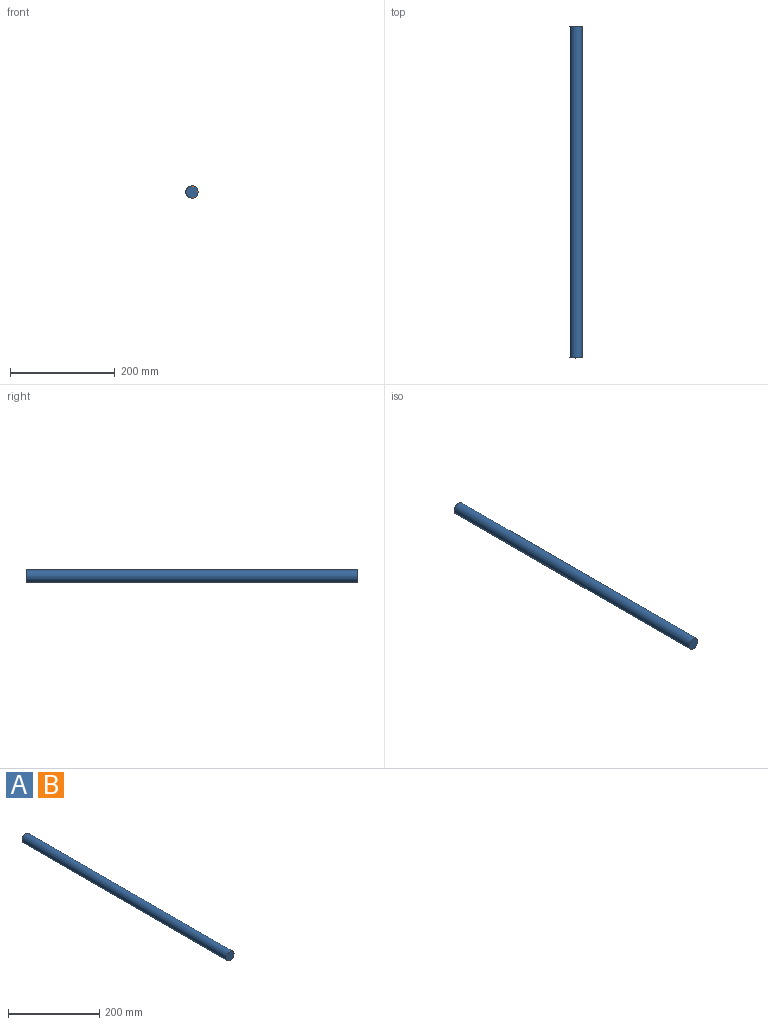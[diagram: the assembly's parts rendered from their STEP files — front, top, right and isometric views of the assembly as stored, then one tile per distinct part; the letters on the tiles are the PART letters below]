
ASSEMBLY  parts=2 mates=1
PART A: 3 faces, bbox 23.6x635x23.6 mm
  f0: cylinder r=11.81mm len=635mm, axis (0,1,0), area 47123.8mm2, adj f1,f2
  f1: plane 23.62x23.62mm, normal (0,-1,0), area 438.3mm2, adj f0
  f2: plane 23.62x23.62mm, normal (0,1,0), area 438.3mm2, adj f0
PART B: same geometry as A
PLACE A t=(185.07,439.59,0)mm
PLACE B t=(185.07,439.59,0)mm
MATE fastened B.f0 <-> A.f0  axis (0,1,0) through (185.07,-195.41,0)mm
